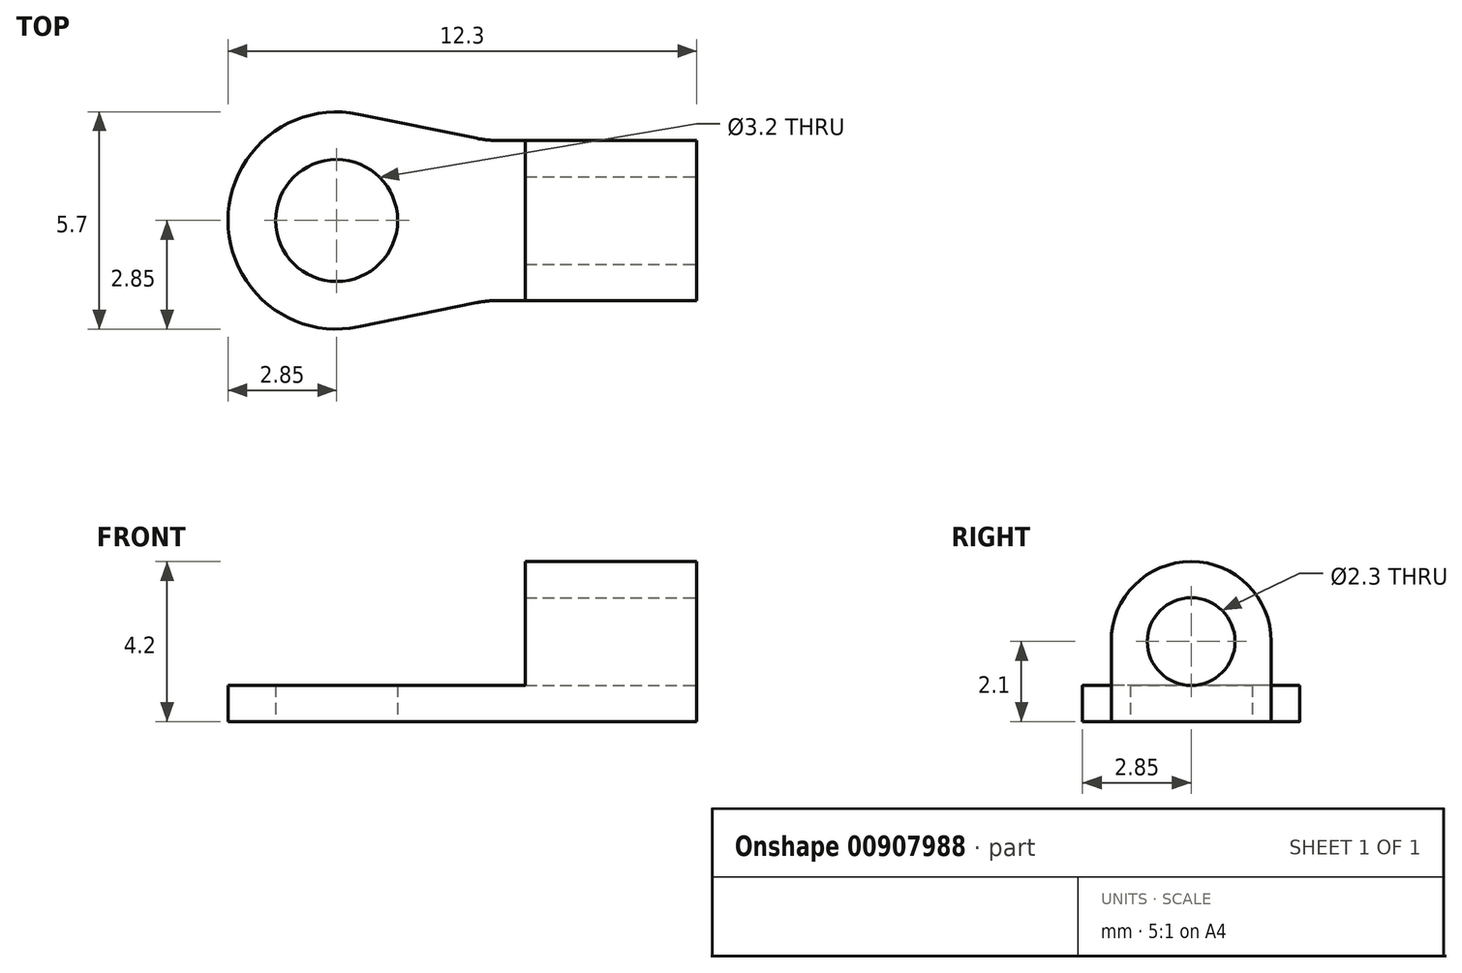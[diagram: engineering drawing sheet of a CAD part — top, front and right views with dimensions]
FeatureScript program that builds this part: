
annotation { "Feature Type Name" : "Feature", "Feature Type Description" : "" }
export const myFeature = defineFeature(function(context is Context, id is Id, definition is map)
    precondition{}
    {
        {
            var Q0;
            Q0=qCreatedBy(makeId("Top.planeOp"),FACE);
            var sketch = newSketch(context, id + "F0", { "sketchPlane" : qUnion([Q0])});
            skLineSegment(sketch, "E0.left", {"start": v(0, 2.85) * mm, "end": v(0, 2.85) * mm});
            skLineSegment(sketch, "E0.right", {"start": v(12.3, 0.75) * mm, "end": v(12.3, 4.95) * mm});
            skLineSegment(sketch, "E1.bottom", {"start": v(12.3, 0.75) * mm, "end": v(7.09, 0.75) * mm});
            skLineSegment(sketch, "E1.top", {"start": v(12.3, 4.95) * mm, "end": v(7.09, 4.95) * mm});
            skPoint(sketch, "E1.middle", {"position": v(12.3, 2.85) * mm});
            skPoint(sketch, "E2.visualSharp", {"position": v(0, 5.7) * mm});
            skArc(sketch, "E2.filletArc", {"start": v(2.85, 5.7) * mm, "mid": v(0.83, 4.87) * mm, "end": v(0, 2.85) * mm});
            skPoint(sketch, "E3.visualSharp", {"position": v(0, 0) * mm});
            skArc(sketch, "E3.filletArc", {"start": v(0, 2.85) * mm, "mid": v(0.83, 0.83) * mm, "end": v(2.85, 0) * mm});
            skArc(sketch, "E4", {"start": v(3.42, 5.64) * mm, "mid": v(0, 2.85) * mm, "end": v(3.42, 0.06) * mm});
            skCircle(sketch, "E5", {"center": v(2.85, 2.85) * mm, "radius": 1.6 * mm});
            skLineSegment(sketch, "E6", {"start": v(6.52, 5) * mm, "end": v(3.42, 5.64) * mm});
            skLineSegment(sketch, "E7", {"start": v(6.52, 0.7) * mm, "end": v(3.42, 0.06) * mm});
            skPoint(sketch, "E8.visualSharp", {"position": v(6.8, 4.95) * mm});
            skArc(sketch, "E8.filletArc", {"start": v(6.52, 5) * mm, "mid": v(6.8, 4.96) * mm, "end": v(7.09, 4.95) * mm});
            skPoint(sketch, "E9.visualSharp", {"position": v(6.8, 0.75) * mm});
            skArc(sketch, "E9.filletArc", {"start": v(7.09, 0.75) * mm, "mid": v(6.8, 0.74) * mm, "end": v(6.52, 0.7) * mm});
            skPoint(sketch, "E10.orphan", {"position": v(16.8, 4.95) * mm});
            skPoint(sketch, "E11.orphan", {"position": v(16.8, 0.75) * mm});
            skPoint(sketch, "E0.top.end.orphan", {"position": v(12.3, 5.7) * mm});
            skPoint(sketch, "E0.bottom.end.orphan", {"position": v(12.3, 0) * mm});
            skPoint(sketch, "E1.right.end.orphan", {"position": v(7.8, 4.95) * mm});
            skPoint(sketch, "E1.right.start.orphan", {"position": v(7.8, 0.75) * mm});
            skSolve(sketch);
        }
        {
            var Q0;
            Q0=makeQuery(id+"F0.imprint","IMPRINT",FACE,{"disambiguationData":[TD([[makeQuery(id+"F0.imprint","IMPRINT",EDGE,{"derivedFrom":sQuery(id+"F0.wireOp",EDGE,"E0.right")}),1.0]])]});
            extrude(context, id + "F1", {"entities" : qUnion([Q0]), "depth" : 0.95 * mm, "offsetDistance" : 25 * mm});
        }
        {
            var Q0;
            Q0=makeQuery(id+"F1.opExtrude","CAP_FACE",FACE,{"disambiguationData":[OSD([sQuery(id+"F0.wireOp",EDGE,"E0.right"),sQuery(id+"F0.wireOp",EDGE,"E1.bottom"),sQuery(id+"F0.wireOp",EDGE,"E1.top"),sQuery(id+"F0.wireOp",EDGE,"E4"),sQuery(id+"F0.wireOp",EDGE,"E5"),sQuery(id+"F0.wireOp",EDGE,"E6"),sQuery(id+"F0.wireOp",EDGE,"E7"),sQuery(id+"F0.wireOp",EDGE,"E8.filletArc"),sQuery(id+"F0.wireOp",EDGE,"E9.filletArc")])],"isStart":false});
            var sketch = newSketch(context, id + "F2", { "sketchPlane" : qUnion([Q0])});
            skLineSegment(sketch, "E12.bottom", {"start": v(12.3, 4.95) * mm, "end": v(7.8, 4.95) * mm});
            skLineSegment(sketch, "E12.top", {"start": v(12.3, 0.75) * mm, "end": v(7.8, 0.75) * mm});
            skLineSegment(sketch, "E12.left", {"start": v(12.3, 4.95) * mm, "end": v(12.3, 0.75) * mm});
            skLineSegment(sketch, "E12.right", {"start": v(7.8, 4.95) * mm, "end": v(7.8, 0.75) * mm});
            skSolve(sketch);
        }
        {
            var Q0;
            Q0=makeQuery(id+"F2.imprint","IMPRINT",FACE,{"disambiguationData":[TD([[makeQuery(id+"F2.imprint","IMPRINT",EDGE,{"derivedFrom":sQuery(id+"F2.wireOp",EDGE,"E12.bottom")}),1.0]])]});
            extrude(context, id + "F3", {"entities" : qUnion([Q0]), "operationType" : NewBodyOperationType.ADD, "depth" : 3.25 * mm, "offsetDistance" : 25 * mm});
        }
        {
            var Q0;
            Q0=makeQuery(id+"F3.opExtrude","CAP_EDGE",EDGE,{"disambiguationData":[OSD([sQuery(id+"F2.wireOp",EDGE,"E12.bottom")])],"isStart":false});
            var Q1;
            Q1=makeQuery(id+"F3.opExtrude","CAP_EDGE",EDGE,{"disambiguationData":[OSD([sQuery(id+"F2.wireOp",EDGE,"E12.top")])],"isStart":false});
            fillet(context, id + "F4", {"entities" : qUnion([Q0, Q1]), "radius" : 2.1 * mm, "tangentPropagation" : true, "allowEdgeOverflow" : false});
        }
        {
            var Q0;
            Q0=makeQuery(id+"F3.boolean.opBoolean","MERGE",FACE,{"derivedFrom":[makeQuery(id+"F1.opExtrude","SWEPT_FACE",FACE,{"disambiguationData":[OSD([sQuery(id+"F0.wireOp",EDGE,"E0.right")])]}),makeQuery(id+"F3.opExtrude","SWEPT_FACE",FACE,{"disambiguationData":[OSD([sQuery(id+"F2.wireOp",EDGE,"E12.left")])]})]});
            var sketch = newSketch(context, id + "F5", { "sketchPlane" : qUnion([Q0])});
            skCircle(sketch, "E13", {"center": v(2.85, 2.1) * mm, "radius": 1.15 * mm});
            skSolve(sketch);
        }
        {
            var Q0;
            Q0=makeQuery(id+"F5.imprint","IMPRINT",FACE,{"disambiguationData":[TD([[makeQuery(id+"F5.imprint","IMPRINT",EDGE,{"derivedFrom":sQuery(id+"F5.wireOp",EDGE,"E13")}),1.0]])]});
            extrude(context, id + "F6", {"entities" : qUnion([Q0]), "operationType" : NewBodyOperationType.REMOVE, "oppositeDirection" : true, "depth" : 25 * mm, "offsetDistance" : 25 * mm});
        }
    });
